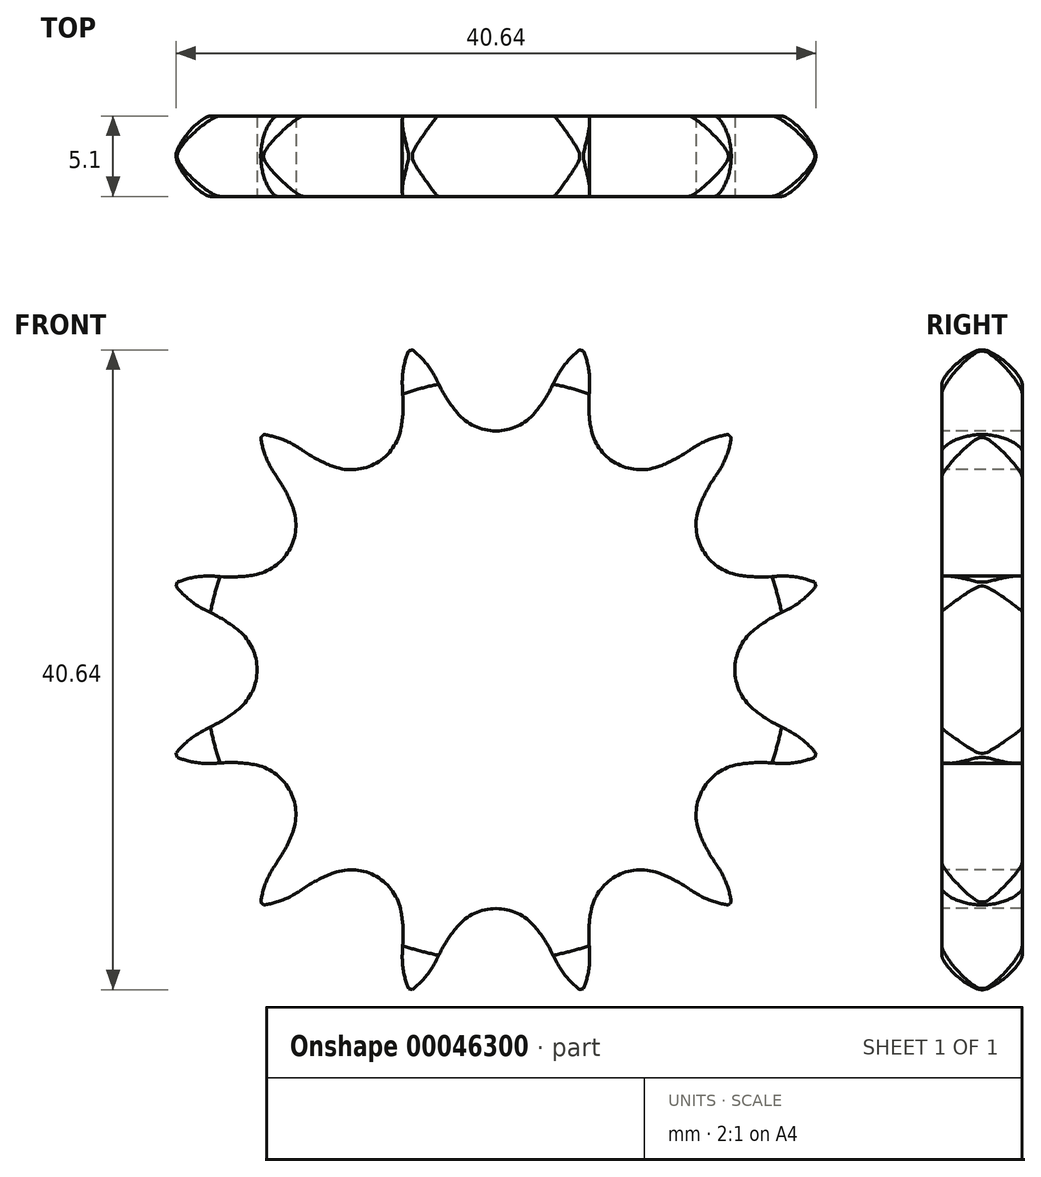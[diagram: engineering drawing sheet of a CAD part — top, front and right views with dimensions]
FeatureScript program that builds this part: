
annotation { "Feature Type Name" : "Feature", "Feature Type Description" : "" }
export const myFeature = defineFeature(function(context is Context, id is Id, definition is map)
    precondition{}
    {
        {
            var Q0;
            Q0=qCreatedBy(makeId("Right.planeOp"),FACE);
            var sketch = newSketch(context, id + "F0", { "sketchPlane" : qUnion([Q0])});
            skLineSegment(sketch, "E0", {"start": v(0, 0) * mm, "end": v(5.1, 0) * mm, "construction": true});
            skLineSegment(sketch, "E1", {"start": v(0, 21) * mm, "end": v(5.1, 21) * mm});
            skLineSegment(sketch, "E2", {"start": v(5.1, 21) * mm, "end": v(5.1, 15) * mm});
            skLineSegment(sketch, "E3", {"start": v(5.1, 15) * mm, "end": v(5.1, 15) * mm});
            skLineSegment(sketch, "E4", {"start": v(5.1, 15) * mm, "end": v(5.1, 0) * mm});
            skLineSegment(sketch, "E5", {"start": v(0, 0) * mm, "end": v(0, 21) * mm});
            skLineSegment(sketch, "E6.0.MirrorCS", {"start": v(0, -21) * mm, "end": v(5.1, -21) * mm});
            skLineSegment(sketch, "E6.1.MirrorCS", {"start": v(5.1, -21) * mm, "end": v(5.1, -15) * mm});
            skLineSegment(sketch, "E6.3.MirrorCS", {"start": v(5.1, -15) * mm, "end": v(5.1, 0) * mm});
            skLineSegment(sketch, "E6.4.MirrorCS", {"start": v(5.1, -15) * mm, "end": v(5.1, -15) * mm});
            skLineSegment(sketch, "E6.5.MirrorCS", {"start": v(0, 0) * mm, "end": v(0, -21) * mm});
            skLineSegment(sketch, "E7", {"start": v(0, 0) * mm, "end": v(5.1, 0) * mm});
            skSolve(sketch);
        }
        {
            var Q0;
            Q0=makeQuery(id+"F0.imprint","IMPRINT",FACE,{"disambiguationData":[TD([[makeQuery(id+"F0.imprint","IMPRINT",EDGE,{"derivedFrom":sQuery(id+"F0.wireOp",EDGE,"E1")}),-1.0]])]});
            var Q1;
            Q1=sQuery(id+"F0.wireOp",EDGE,"E0");
            revolve(context, id + "F1", {"entities" : qUnion([Q0]), "axis" : qUnion([Q1]), "revolveType" : RevolveType.FULL});
        }
        {
            var Q0;
            Q0=makeQuery(id+"F1.opRevolve","SWEPT_EDGE",EDGE,{"disambiguationData":[OSD([sQuery(id+"F0.wireOp",EDGE,"E1"),sQuery(id+"F0.wireOp",EDGE,"E5")])]});
            var Q1;
            Q1=makeQuery(id+"F1.opRevolve","SWEPT_EDGE",EDGE,{"disambiguationData":[OSD([sQuery(id+"F0.wireOp",EDGE,"E1"),sQuery(id+"F0.wireOp",EDGE,"E2")])]});
            fillet(context, id + "F2", {"entities" : qUnion([Q0, Q1]), "radius" : 2.5 * mm, "tangentPropagation" : true, "rho" : 0.2, "crossSection" : FilletCrossSection.CONIC, "allowEdgeOverflow" : false});
        }
        {
            var Q0;
            Q0=makeQuery(id+"F1.opRevolve","SWEPT_FACE",FACE,{"disambiguationData":[OSD([sQuery(id+"F0.wireOp",EDGE,"E5")])]});
            var sketch = newSketch(context, id + "F3", { "sketchPlane" : qUnion([Q0])});
            skArc(sketch, "E8", {"start": v(-5.48, 20.44) * mm, "mid": v(-12.65, 12.63) * mm, "end": v(-3.81, 18.5) * mm, "construction": true});
            skLineSegment(sketch, "E9", {"start": v(2.95, 5.03) * mm, "end": v(-3.81, 18.5) * mm, "construction": true});
            skArc(sketch, "E10", {"start": v(-2.47, 16.33) * mm, "mid": v(10.83, 26.23) * mm, "end": v(-3.53, 17.94) * mm, "construction": true});
            skArc(sketch, "E11", {"start": v(2.47, 16.33) * mm, "mid": v(0, 21.63) * mm, "end": v(-2.47, 16.33) * mm, "construction": true});
            skLineSegment(sketch, "E12", {"start": v(0, 0) * mm, "end": v(7.34, 0) * mm, "construction": true});
            skLineSegment(sketch, "E13", {"start": v(0, 18.4) * mm, "end": v(74.94, 18.4) * mm, "construction": true});
            skLineSegment(sketch, "E14", {"start": v(3.9, 21.67) * mm, "end": v(-3.53, 17.94) * mm, "construction": true});
            skLineSegment(sketch, "E15", {"start": v(0, 0) * mm, "end": v(-5.48, 20.44) * mm, "construction": true});
            skLineSegment(sketch, "E16", {"start": v(0, 0) * mm, "end": v(0, 18.4) * mm, "construction": true});
            skCircle(sketch, "E17", {"center": v(0, 0) * mm, "radius": 18.4 * mm, "construction": true});
            skLineSegment(sketch, "E18", {"start": v(0, 18.4) * mm, "end": v(3.9, 21.67) * mm, "construction": true});
            skArc(sketch, "E19", {"start": v(-2.47, 16.33) * mm, "mid": v(0, 15.17) * mm, "end": v(2.47, 16.33) * mm});
            skArc(sketch, "E20", {"start": v(-3.81, 18.5) * mm, "mid": v(-4.53, 19.57) * mm, "end": v(-5.48, 20.44) * mm});
            skArc(sketch, "E21.0.MirrorCS", {"start": v(3.53, 17.94) * mm, "mid": v(3.05, 17.1) * mm, "end": v(2.47, 16.33) * mm});
            skLineSegment(sketch, "E22.0.MirrorCS", {"start": v(3.53, 17.94) * mm, "end": v(3.81, 18.5) * mm});
            skArc(sketch, "E23.0.MirrorCS", {"start": v(3.81, 18.5) * mm, "mid": v(4.53, 19.57) * mm, "end": v(5.48, 20.44) * mm});
            skArc(sketch, "E24", {"start": v(-3.53, 17.94) * mm, "mid": v(-3.05, 17.1) * mm, "end": v(-2.47, 16.33) * mm});
            skLineSegment(sketch, "E25", {"start": v(-3.53, 17.94) * mm, "end": v(-3.81, 18.5) * mm});
            skArc(sketch, "E26.1.0", {"start": v(-12.55, 14.11) * mm, "mid": v(-13.7, 14.68) * mm, "end": v(-14.96, 14.96) * mm});
            skLineSegment(sketch, "E26.1.1", {"start": v(-12.03, 13.77) * mm, "end": v(-12.55, 14.11) * mm});
            skArc(sketch, "E26.1.2", {"start": v(-12.03, 13.77) * mm, "mid": v(-11.2, 13.28) * mm, "end": v(-10.3, 12.9) * mm});
            skArc(sketch, "E26.1.3", {"start": v(-10.3, 12.9) * mm, "mid": v(-7.59, 13.14) * mm, "end": v(-6.02, 15.37) * mm});
            skArc(sketch, "E26.1.4", {"start": v(-5.9, 17.3) * mm, "mid": v(-5.9, 16.33) * mm, "end": v(-6.02, 15.37) * mm});
            skLineSegment(sketch, "E26.1.5", {"start": v(-5.9, 17.3) * mm, "end": v(-5.95, 17.93) * mm});
            skArc(sketch, "E26.1.6", {"start": v(-5.95, 17.93) * mm, "mid": v(-5.86, 19.21) * mm, "end": v(-5.48, 20.44) * mm});
            skArc(sketch, "E26.2.0", {"start": v(-17.93, 5.95) * mm, "mid": v(-19.21, 5.86) * mm, "end": v(-20.44, 5.48) * mm});
            skLineSegment(sketch, "E26.2.1", {"start": v(-17.3, 5.9) * mm, "end": v(-17.93, 5.95) * mm});
            skArc(sketch, "E26.2.2", {"start": v(-17.3, 5.9) * mm, "mid": v(-16.33, 5.9) * mm, "end": v(-15.37, 6.02) * mm});
            skArc(sketch, "E26.2.3", {"start": v(-15.37, 6.02) * mm, "mid": v(-13.14, 7.59) * mm, "end": v(-12.9, 10.3) * mm});
            skArc(sketch, "E26.2.4", {"start": v(-13.77, 12.03) * mm, "mid": v(-13.28, 11.2) * mm, "end": v(-12.9, 10.3) * mm});
            skLineSegment(sketch, "E26.2.5", {"start": v(-13.77, 12.03) * mm, "end": v(-14.11, 12.55) * mm});
            skArc(sketch, "E26.2.6", {"start": v(-14.11, 12.55) * mm, "mid": v(-14.68, 13.7) * mm, "end": v(-14.96, 14.96) * mm});
            skArc(sketch, "E26.3.0", {"start": v(-18.5, -3.81) * mm, "mid": v(-19.57, -4.53) * mm, "end": v(-20.44, -5.48) * mm});
            skLineSegment(sketch, "E26.3.1", {"start": v(-17.94, -3.53) * mm, "end": v(-18.5, -3.81) * mm});
            skArc(sketch, "E26.3.2", {"start": v(-17.94, -3.53) * mm, "mid": v(-17.1, -3.05) * mm, "end": v(-16.33, -2.47) * mm});
            skArc(sketch, "E26.3.3", {"start": v(-16.33, -2.47) * mm, "mid": v(-15.17, 0) * mm, "end": v(-16.33, 2.47) * mm});
            skArc(sketch, "E26.3.4", {"start": v(-17.94, 3.53) * mm, "mid": v(-17.1, 3.05) * mm, "end": v(-16.33, 2.47) * mm});
            skLineSegment(sketch, "E26.3.5", {"start": v(-17.94, 3.53) * mm, "end": v(-18.5, 3.81) * mm});
            skArc(sketch, "E26.3.6", {"start": v(-18.5, 3.81) * mm, "mid": v(-19.57, 4.53) * mm, "end": v(-20.44, 5.48) * mm});
            skArc(sketch, "E26.4.0", {"start": v(-14.11, -12.55) * mm, "mid": v(-14.68, -13.7) * mm, "end": v(-14.96, -14.96) * mm});
            skLineSegment(sketch, "E26.4.1", {"start": v(-13.77, -12.03) * mm, "end": v(-14.11, -12.55) * mm});
            skArc(sketch, "E26.4.2", {"start": v(-13.77, -12.03) * mm, "mid": v(-13.28, -11.2) * mm, "end": v(-12.9, -10.3) * mm});
            skArc(sketch, "E26.4.3", {"start": v(-12.9, -10.3) * mm, "mid": v(-13.14, -7.59) * mm, "end": v(-15.37, -6.02) * mm});
            skArc(sketch, "E26.4.4", {"start": v(-17.3, -5.9) * mm, "mid": v(-16.33, -5.9) * mm, "end": v(-15.37, -6.02) * mm});
            skLineSegment(sketch, "E26.4.5", {"start": v(-17.3, -5.9) * mm, "end": v(-17.93, -5.95) * mm});
            skArc(sketch, "E26.4.6", {"start": v(-17.93, -5.95) * mm, "mid": v(-19.21, -5.86) * mm, "end": v(-20.44, -5.48) * mm});
            skArc(sketch, "E26.5.0", {"start": v(-5.95, -17.93) * mm, "mid": v(-5.86, -19.21) * mm, "end": v(-5.48, -20.44) * mm});
            skLineSegment(sketch, "E26.5.1", {"start": v(-5.9, -17.3) * mm, "end": v(-5.95, -17.93) * mm});
            skArc(sketch, "E26.5.2", {"start": v(-5.9, -17.3) * mm, "mid": v(-5.9, -16.33) * mm, "end": v(-6.02, -15.37) * mm});
            skArc(sketch, "E26.5.3", {"start": v(-6.02, -15.37) * mm, "mid": v(-7.59, -13.14) * mm, "end": v(-10.3, -12.9) * mm});
            skArc(sketch, "E26.5.4", {"start": v(-12.03, -13.77) * mm, "mid": v(-11.2, -13.28) * mm, "end": v(-10.3, -12.9) * mm});
            skLineSegment(sketch, "E26.5.5", {"start": v(-12.03, -13.77) * mm, "end": v(-12.55, -14.11) * mm});
            skArc(sketch, "E26.5.6", {"start": v(-12.55, -14.11) * mm, "mid": v(-13.7, -14.68) * mm, "end": v(-14.96, -14.96) * mm});
            skArc(sketch, "E26.6.0", {"start": v(3.81, -18.5) * mm, "mid": v(4.53, -19.57) * mm, "end": v(5.48, -20.44) * mm});
            skLineSegment(sketch, "E26.6.1", {"start": v(3.53, -17.94) * mm, "end": v(3.81, -18.5) * mm});
            skArc(sketch, "E26.6.2", {"start": v(3.53, -17.94) * mm, "mid": v(3.05, -17.1) * mm, "end": v(2.47, -16.33) * mm});
            skArc(sketch, "E26.6.3", {"start": v(2.47, -16.33) * mm, "mid": v(0, -15.17) * mm, "end": v(-2.47, -16.33) * mm});
            skArc(sketch, "E26.6.4", {"start": v(-3.53, -17.94) * mm, "mid": v(-3.05, -17.1) * mm, "end": v(-2.47, -16.33) * mm});
            skLineSegment(sketch, "E26.6.5", {"start": v(-3.53, -17.94) * mm, "end": v(-3.81, -18.5) * mm});
            skArc(sketch, "E26.6.6", {"start": v(-3.81, -18.5) * mm, "mid": v(-4.53, -19.57) * mm, "end": v(-5.48, -20.44) * mm});
            skArc(sketch, "E26.7.0", {"start": v(12.55, -14.11) * mm, "mid": v(13.7, -14.68) * mm, "end": v(14.96, -14.96) * mm});
            skLineSegment(sketch, "E26.7.1", {"start": v(12.03, -13.77) * mm, "end": v(12.55, -14.11) * mm});
            skArc(sketch, "E26.7.2", {"start": v(12.03, -13.77) * mm, "mid": v(11.2, -13.28) * mm, "end": v(10.3, -12.9) * mm});
            skArc(sketch, "E26.7.3", {"start": v(10.3, -12.9) * mm, "mid": v(7.59, -13.14) * mm, "end": v(6.02, -15.37) * mm});
            skArc(sketch, "E26.7.4", {"start": v(5.9, -17.3) * mm, "mid": v(5.9, -16.33) * mm, "end": v(6.02, -15.37) * mm});
            skLineSegment(sketch, "E26.7.5", {"start": v(5.9, -17.3) * mm, "end": v(5.95, -17.93) * mm});
            skArc(sketch, "E26.7.6", {"start": v(5.95, -17.93) * mm, "mid": v(5.86, -19.21) * mm, "end": v(5.48, -20.44) * mm});
            skArc(sketch, "E26.8.0", {"start": v(17.93, -5.95) * mm, "mid": v(19.21, -5.86) * mm, "end": v(20.44, -5.48) * mm});
            skLineSegment(sketch, "E26.8.1", {"start": v(17.3, -5.9) * mm, "end": v(17.93, -5.95) * mm});
            skArc(sketch, "E26.8.2", {"start": v(17.3, -5.9) * mm, "mid": v(16.33, -5.9) * mm, "end": v(15.37, -6.02) * mm});
            skArc(sketch, "E26.8.3", {"start": v(15.37, -6.02) * mm, "mid": v(13.14, -7.59) * mm, "end": v(12.9, -10.3) * mm});
            skArc(sketch, "E26.8.4", {"start": v(13.77, -12.03) * mm, "mid": v(13.28, -11.2) * mm, "end": v(12.9, -10.3) * mm});
            skLineSegment(sketch, "E26.8.5", {"start": v(13.77, -12.03) * mm, "end": v(14.11, -12.55) * mm});
            skArc(sketch, "E26.8.6", {"start": v(14.11, -12.55) * mm, "mid": v(14.68, -13.7) * mm, "end": v(14.96, -14.96) * mm});
            skArc(sketch, "E26.9.0", {"start": v(18.5, 3.81) * mm, "mid": v(19.57, 4.53) * mm, "end": v(20.44, 5.48) * mm});
            skLineSegment(sketch, "E26.9.1", {"start": v(17.94, 3.53) * mm, "end": v(18.5, 3.81) * mm});
            skArc(sketch, "E26.9.2", {"start": v(17.94, 3.53) * mm, "mid": v(17.1, 3.05) * mm, "end": v(16.33, 2.47) * mm});
            skArc(sketch, "E26.9.3", {"start": v(16.33, 2.47) * mm, "mid": v(15.17, 0) * mm, "end": v(16.33, -2.47) * mm});
            skArc(sketch, "E26.9.4", {"start": v(17.94, -3.53) * mm, "mid": v(17.1, -3.05) * mm, "end": v(16.33, -2.47) * mm});
            skLineSegment(sketch, "E26.9.5", {"start": v(17.94, -3.53) * mm, "end": v(18.5, -3.81) * mm});
            skArc(sketch, "E26.9.6", {"start": v(18.5, -3.81) * mm, "mid": v(19.57, -4.53) * mm, "end": v(20.44, -5.48) * mm});
            skArc(sketch, "E26.10.0", {"start": v(14.11, 12.55) * mm, "mid": v(14.68, 13.7) * mm, "end": v(14.96, 14.96) * mm});
            skLineSegment(sketch, "E26.10.1", {"start": v(13.77, 12.03) * mm, "end": v(14.11, 12.55) * mm});
            skArc(sketch, "E26.10.2", {"start": v(13.77, 12.03) * mm, "mid": v(13.28, 11.2) * mm, "end": v(12.9, 10.3) * mm});
            skArc(sketch, "E26.10.3", {"start": v(12.9, 10.3) * mm, "mid": v(13.14, 7.59) * mm, "end": v(15.37, 6.02) * mm});
            skArc(sketch, "E26.10.4", {"start": v(17.3, 5.9) * mm, "mid": v(16.33, 5.9) * mm, "end": v(15.37, 6.02) * mm});
            skLineSegment(sketch, "E26.10.5", {"start": v(17.3, 5.9) * mm, "end": v(17.93, 5.95) * mm});
            skArc(sketch, "E26.10.6", {"start": v(17.93, 5.95) * mm, "mid": v(19.21, 5.86) * mm, "end": v(20.44, 5.48) * mm});
            skArc(sketch, "E26.11.0", {"start": v(5.95, 17.93) * mm, "mid": v(5.86, 19.21) * mm, "end": v(5.48, 20.44) * mm});
            skLineSegment(sketch, "E26.11.1", {"start": v(5.9, 17.3) * mm, "end": v(5.95, 17.93) * mm});
            skArc(sketch, "E26.11.2", {"start": v(5.9, 17.3) * mm, "mid": v(5.9, 16.33) * mm, "end": v(6.02, 15.37) * mm});
            skArc(sketch, "E26.11.3", {"start": v(6.02, 15.37) * mm, "mid": v(7.59, 13.14) * mm, "end": v(10.3, 12.9) * mm});
            skArc(sketch, "E26.11.4", {"start": v(12.03, 13.77) * mm, "mid": v(11.2, 13.28) * mm, "end": v(10.3, 12.9) * mm});
            skLineSegment(sketch, "E26.11.5", {"start": v(12.03, 13.77) * mm, "end": v(12.55, 14.11) * mm});
            skArc(sketch, "E26.11.6", {"start": v(12.55, 14.11) * mm, "mid": v(13.7, 14.68) * mm, "end": v(14.96, 14.96) * mm});
            skSolve(sketch);
        }
        {
            var Q0;
            Q0 = qSketchRegion(id + "F3", true);
            extrude(context, id + "F4", {"entities" : qUnion([Q0]), "operationType" : NewBodyOperationType.INTERSECT, "endBound" : BoundingType.THROUGH_ALL, "oppositeDirection" : true, "depth" : 25.4 * mm});
        }
    });
